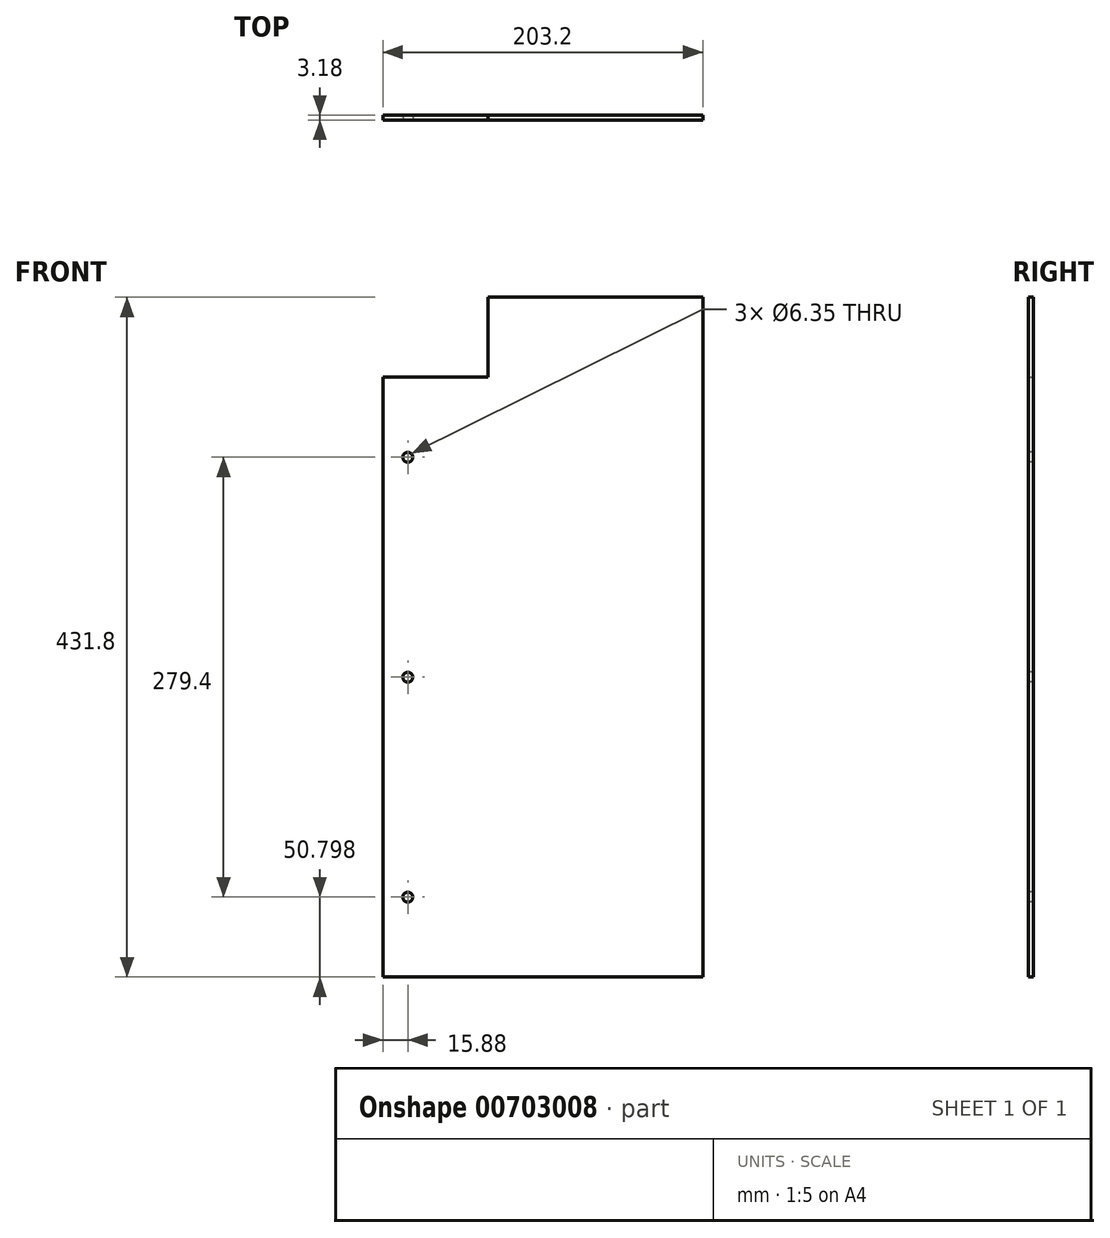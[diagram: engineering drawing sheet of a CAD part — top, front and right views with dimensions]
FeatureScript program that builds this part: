
annotation { "Feature Type Name" : "Feature", "Feature Type Description" : "" }
export const myFeature = defineFeature(function(context is Context, id is Id, definition is map)
    precondition{}
    {
        {
            var Q0;
            Q0=qCreatedBy(makeId("Front.planeOp"),FACE);
            var sketch = newSketch(context, id + "F0", { "sketchPlane" : qUnion([Q0])});
            skLineSegment(sketch, "E0.top", {"start": v(-157.18, -57.45) * mm, "end": v(46.02, -57.45) * mm});
            skLineSegment(sketch, "E0.right", {"start": v(46.02, 374.35) * mm, "end": v(46.02, -57.45) * mm});
            skLineSegment(sketch, "E1", {"start": v(-90.5, 374.35) * mm, "end": v(-90.5, 323.55) * mm});
            skLineSegment(sketch, "E2", {"start": v(-90.5, 323.55) * mm, "end": v(-157.18, 323.55) * mm});
            skLineSegment(sketch, "E3", {"start": v(-90.5, 374.35) * mm, "end": v(46.02, 374.35) * mm});
            skLineSegment(sketch, "E4", {"start": v(-157.18, 323.55) * mm, "end": v(-157.18, -57.45) * mm});
            skSolve(sketch);
        }
        {
            var Q0;
            Q0=makeQuery(id+"F0.imprint","IMPRINT",FACE,{"disambiguationData":[TD([[makeQuery(id+"F0.imprint","IMPRINT",EDGE,{"derivedFrom":sQuery(id+"F0.wireOp",EDGE,"E0.top")}),1.0]])]});
            extrude(context, id + "F1", {"entities" : qUnion([Q0]), "depth" : 3.17 * mm, "offsetDistance" : 25.4 * mm});
        }
        {
            var Q0;
            Q0=makeQuery(id+"F1.opExtrude","CAP_FACE",FACE,{"disambiguationData":[OSD([sQuery(id+"F0.wireOp",EDGE,"E0.top"),sQuery(id+"F0.wireOp",EDGE,"E0.right"),sQuery(id+"F0.wireOp",EDGE,"E1"),sQuery(id+"F0.wireOp",EDGE,"E2"),sQuery(id+"F0.wireOp",EDGE,"E3"),sQuery(id+"F0.wireOp",EDGE,"E4")])],"isStart":false});
            var sketch = newSketch(context, id + "F2", { "sketchPlane" : qUnion([Q0])});
            skLineSegment(sketch, "E5", {"start": v(-157.18, 323.55) * mm, "end": v(-141.3, 323.55) * mm});
            skLineSegment(sketch, "E6", {"start": v(-141.3, 323.55) * mm, "end": v(-141.3, -57.45) * mm});
            skLineSegment(sketch, "E7", {"start": v(-141.3, 323.55) * mm, "end": v(-141.3, 272.75) * mm});
            skLineSegment(sketch, "E8", {"start": v(-141.3, -57.45) * mm, "end": v(-141.3, -6.65) * mm});
            skCircle(sketch, "E9", {"center": v(-141.3, -6.65) * mm, "radius": 1.59 * mm});
            skCircle(sketch, "E10", {"center": v(-141.3, 133.05) * mm, "radius": 1.59 * mm});
            skCircle(sketch, "E11", {"center": v(-141.3, 272.75) * mm, "radius": 1.59 * mm});
            skSolve(sketch);
        }
        {
            var Q0;
            Q0=sQuery(id+"F2.wireOp",VERTEX,"E9.center");
            var Q1;
            Q1=makeQuery(id+"F1.opExtrude","SWEPT_BODY",BODY,{"disambiguationData":[OSD([sQuery(id+"F0.wireOp",EDGE,"E0.top"),sQuery(id+"F0.wireOp",EDGE,"E0.right"),sQuery(id+"F0.wireOp",EDGE,"E1"),sQuery(id+"F0.wireOp",EDGE,"E2"),sQuery(id+"F0.wireOp",EDGE,"E3"),sQuery(id+"F0.wireOp",EDGE,"E4")])]});
            hole(context, id + "F3", {"style" : HoleStyle.SIMPLE, "endStyle" : HoleEndStyle.THROUGH, "holeDiameter" : 6.35 * mm, "majorDiameter" : 6.35 * mm, "isTappedThrough" : true, "tappedDepth" : 12.7 * mm, "tapClearance" : 3, "locations" : qUnion([Q0]), "scope" : qUnion([Q1])});
        }
        {
            var Q0;
            Q0=sQuery(id+"F2.wireOp",VERTEX,"E10.center");
            var Q1;
            Q1=sQuery(id+"F2.wireOp",VERTEX,"E7.end");
            var Q2;
            Q2=makeQuery(id+"F1.opExtrude","SWEPT_BODY",BODY,{"disambiguationData":[OSD([sQuery(id+"F0.wireOp",EDGE,"E0.top"),sQuery(id+"F0.wireOp",EDGE,"E0.right"),sQuery(id+"F0.wireOp",EDGE,"E1"),sQuery(id+"F0.wireOp",EDGE,"E2"),sQuery(id+"F0.wireOp",EDGE,"E3"),sQuery(id+"F0.wireOp",EDGE,"E4")])]});
            hole(context, id + "F4", {"style" : HoleStyle.SIMPLE, "endStyle" : HoleEndStyle.THROUGH, "holeDiameter" : 6.35 * mm, "majorDiameter" : 6.35 * mm, "isTappedThrough" : true, "tappedDepth" : 12.7 * mm, "tapClearance" : 3, "locations" : qUnion([Q0, Q1]), "scope" : qUnion([Q2])});
        }
    });
